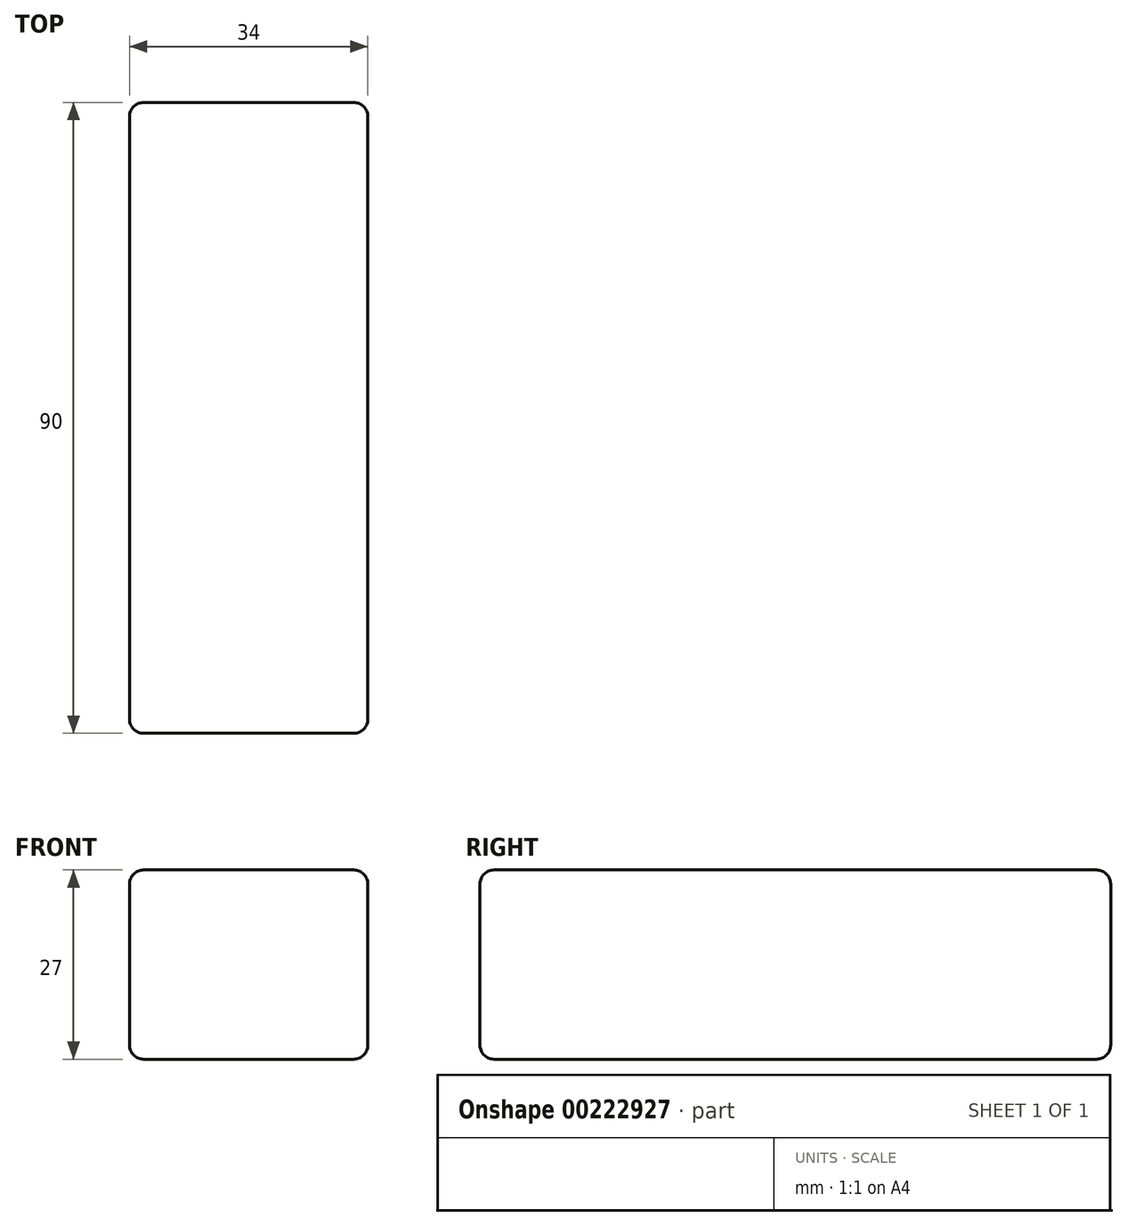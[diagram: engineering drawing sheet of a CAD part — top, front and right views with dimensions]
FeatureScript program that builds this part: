
annotation { "Feature Type Name" : "Feature", "Feature Type Description" : "" }
export const myFeature = defineFeature(function(context is Context, id is Id, definition is map)
    precondition{}
    {
        {
            var Q0;
            Q0=qCreatedBy(makeId("Top.planeOp"),FACE);
            var sketch = newSketch(context, id + "F0", { "sketchPlane" : qUnion([Q0])});
            skLineSegment(sketch, "E0.bottom", {"start": v(-17, 45) * mm, "end": v(17, 45) * mm});
            skLineSegment(sketch, "E0.top", {"start": v(-17, -45) * mm, "end": v(17, -45) * mm});
            skLineSegment(sketch, "E0.left", {"start": v(-17, 45) * mm, "end": v(-17, -45) * mm});
            skLineSegment(sketch, "E0.right", {"start": v(17, 45) * mm, "end": v(17, -45) * mm});
            skPoint(sketch, "E0.middle", {"position": v(0, 0) * mm});
            skSolve(sketch);
        }
        {
            var Q0;
            Q0=makeQuery(id+"F0.imprint","IMPRINT",FACE,{"disambiguationData":[TD([[makeQuery(id+"F0.imprint","IMPRINT",EDGE,{"derivedFrom":sQuery(id+"F0.wireOp",EDGE,"E0.bottom")}),-1.0]])]});
            extrude(context, id + "F1", {"entities" : qUnion([Q0]), "depth" : 27 * mm});
        }
        {
            var Q0;
            Q0=makeQuery(id+"F1.opExtrude","SWEPT_EDGE",EDGE,{"disambiguationData":[OSD([sQuery(id+"F0.wireOp",EDGE,"E0.bottom"),sQuery(id+"F0.wireOp",EDGE,"E0.left")])]});
            var Q1;
            Q1=makeQuery(id+"F1.opExtrude","CAP_EDGE",EDGE,{"disambiguationData":[OSD([sQuery(id+"F0.wireOp",EDGE,"E0.left")])],"isStart":false});
            var Q2;
            Q2=makeQuery(id+"F1.opExtrude","CAP_EDGE",EDGE,{"disambiguationData":[OSD([sQuery(id+"F0.wireOp",EDGE,"E0.bottom")])],"isStart":false});
            var Q3;
            Q3=makeQuery(id+"F1.opExtrude","CAP_EDGE",EDGE,{"disambiguationData":[OSD([sQuery(id+"F0.wireOp",EDGE,"E0.left")])],"isStart":true});
            var Q4;
            Q4=makeQuery(id+"F1.opExtrude","CAP_EDGE",EDGE,{"disambiguationData":[OSD([sQuery(id+"F0.wireOp",EDGE,"E0.bottom")])],"isStart":true});
            var Q5;
            Q5=makeQuery(id+"F1.opExtrude","SWEPT_EDGE",EDGE,{"disambiguationData":[OSD([sQuery(id+"F0.wireOp",EDGE,"E0.bottom"),sQuery(id+"F0.wireOp",EDGE,"E0.right")])]});
            var Q6;
            Q6=makeQuery(id+"F1.opExtrude","CAP_EDGE",EDGE,{"disambiguationData":[OSD([sQuery(id+"F0.wireOp",EDGE,"E0.right")])],"isStart":false});
            var Q7;
            Q7=makeQuery(id+"F1.opExtrude","SWEPT_EDGE",EDGE,{"disambiguationData":[OSD([sQuery(id+"F0.wireOp",EDGE,"E0.top"),sQuery(id+"F0.wireOp",EDGE,"E0.left")])]});
            var Q8;
            Q8=makeQuery(id+"F1.opExtrude","CAP_EDGE",EDGE,{"disambiguationData":[OSD([sQuery(id+"F0.wireOp",EDGE,"E0.top")])],"isStart":false});
            var Q9;
            Q9=makeQuery(id+"F1.opExtrude","CAP_EDGE",EDGE,{"disambiguationData":[OSD([sQuery(id+"F0.wireOp",EDGE,"E0.right")])],"isStart":true});
            var Q10;
            Q10=makeQuery(id+"F1.opExtrude","SWEPT_EDGE",EDGE,{"disambiguationData":[OSD([sQuery(id+"F0.wireOp",EDGE,"E0.top"),sQuery(id+"F0.wireOp",EDGE,"E0.right")])]});
            var Q11;
            Q11=makeQuery(id+"F1.opExtrude","CAP_EDGE",EDGE,{"disambiguationData":[OSD([sQuery(id+"F0.wireOp",EDGE,"E0.top")])],"isStart":true});
            fillet(context, id + "F2", {"entities" : qUnion([Q0, Q1, Q2, Q3, Q4, Q5, Q6, Q7, Q8, Q9, Q10, Q11]), "radius" : 2 * mm, "tangentPropagation" : true, "allowEdgeOverflow" : false});
        }
    });
